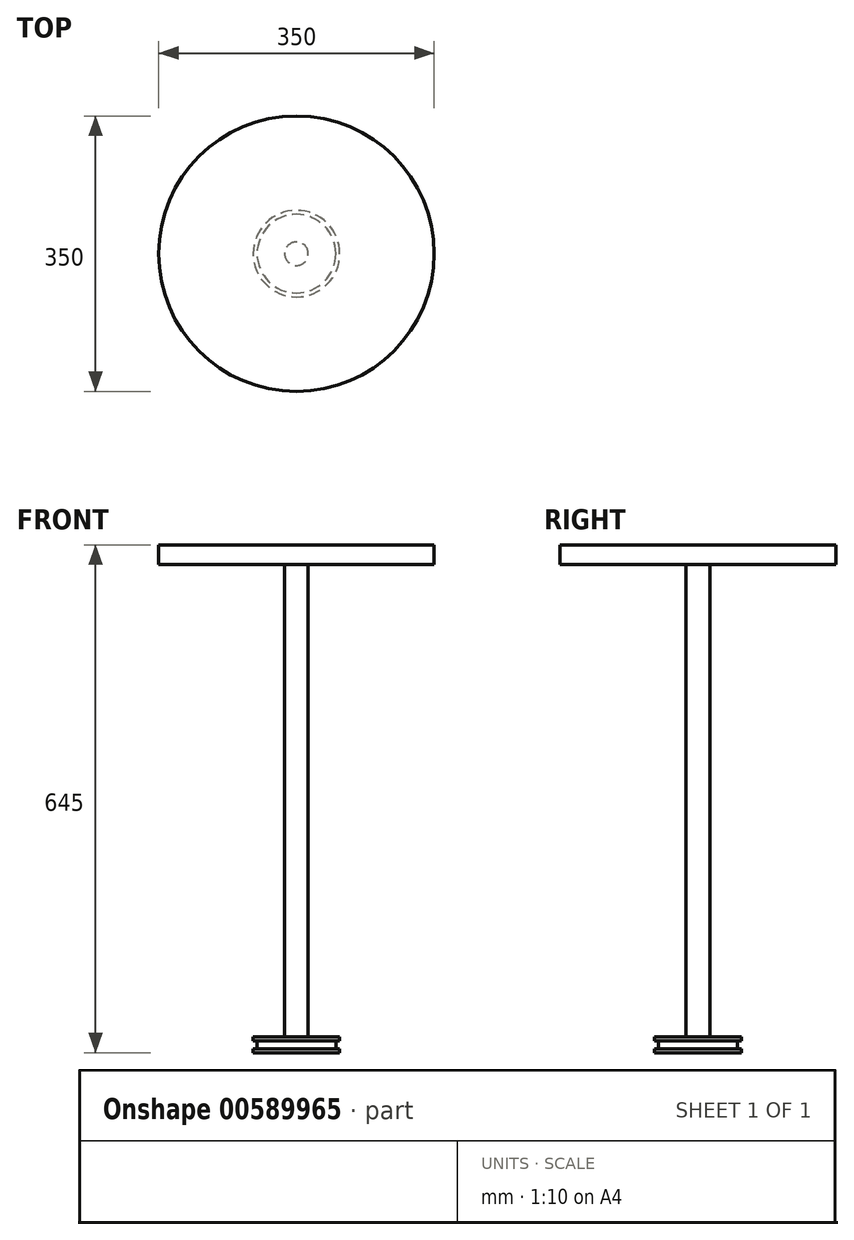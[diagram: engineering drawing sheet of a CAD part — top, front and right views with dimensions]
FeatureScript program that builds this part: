
annotation { "Feature Type Name" : "Feature", "Feature Type Description" : "" }
export const myFeature = defineFeature(function(context is Context, id is Id, definition is map)
    precondition{}
    {
        {
            var Q0;
            Q0=qCreatedBy(makeId("Top.planeOp"),FACE);
            var sketch = newSketch(context, id + "F0", { "sketchPlane" : qUnion([Q0])});
            skCircle(sketch, "E0", {"center": v(0, 0) * mm, "radius": 175 * mm});
            skSolve(sketch);
        }
        {
            var Q0;
            Q0 = qSketchRegion(id + "F0", true);
            extrude(context, id + "F1", {"entities" : qUnion([Q0]), "depth" : 25 * mm, "offsetDistance" : 25 * mm});
        }
        {
            var Q0;
            Q0=makeQuery(id+"F1.opExtrude","CAP_FACE",FACE,{"disambiguationData":[OSD([sQuery(id+"F0.wireOp",EDGE,"E0")])],"isStart":true});
            var sketch = newSketch(context, id + "F2", { "sketchPlane" : qUnion([Q0])});
            skCircle(sketch, "E1", {"center": v(0, 0) * mm, "radius": 15 * mm});
            skSolve(sketch);
        }
        {
            var Q0;
            Q0=makeQuery(id+"F2.imprint","IMPRINT",FACE,{"disambiguationData":[TD([[makeQuery(id+"F2.imprint","IMPRINT",EDGE,{"derivedFrom":sQuery(id+"F2.wireOp",EDGE,"E1")}),1.0]])]});
            extrude(context, id + "F3", {"entities" : qUnion([Q0]), "operationType" : NewBodyOperationType.ADD, "depth" : 600 * mm, "offsetDistance" : 25 * mm});
        }
        {
            var Q0;
            Q0=makeQuery(id+"F3.opExtrude","CAP_FACE",FACE,{"disambiguationData":[OSD([sQuery(id+"F2.wireOp",EDGE,"E1")])],"isStart":false});
            var sketch = newSketch(context, id + "F4", { "sketchPlane" : qUnion([Q0])});
            skCircle(sketch, "E2", {"center": v(0, 0) * mm, "radius": 55 * mm});
            skSolve(sketch);
        }
        {
            var Q0;
            Q0=makeQuery(id+"F4.imprint","IMPRINT",FACE,{"disambiguationData":[TD([[makeQuery(id+"F4.imprint","IMPRINT",EDGE,{"derivedFrom":makeQuery(id+"F3.opExtrude","CAP_EDGE",EDGE,{"disambiguationData":[OSD([sQuery(id+"F2.wireOp",EDGE,"E1")])],"isStart":false})}),1.0]])]});
            var Q1;
            Q1=makeQuery(id+"F4.imprint","IMPRINT",FACE,{"disambiguationData":[TD([[makeQuery(id+"F4.imprint","IMPRINT",EDGE,{"derivedFrom":sQuery(id+"F4.wireOp",EDGE,"E2")}),1.0]])]});
            extrude(context, id + "F5", {"entities" : qUnion([Q0, Q1]), "operationType" : NewBodyOperationType.ADD, "depth" : 5 * mm, "offsetDistance" : 25 * mm});
        }
        {
            var Q0;
            Q0=makeQuery(id+"F5.opExtrude","CAP_FACE",FACE,{"disambiguationData":[OSD([sQuery(id+"F4.wireOp",EDGE,"E2")])],"isStart":false});
            var sketch = newSketch(context, id + "F6", { "sketchPlane" : qUnion([Q0])});
            skCircle(sketch, "E3", {"center": v(0, 0) * mm, "radius": 50 * mm});
            skSolve(sketch);
        }
        {
            var Q0;
            Q0=makeQuery(id+"F6.imprint","IMPRINT",FACE,{"disambiguationData":[TD([[makeQuery(id+"F6.imprint","IMPRINT",EDGE,{"derivedFrom":sQuery(id+"F6.wireOp",EDGE,"E3")}),1.0]])]});
            extrude(context, id + "F7", {"entities" : qUnion([Q0]), "operationType" : NewBodyOperationType.ADD, "depth" : 10 * mm, "offsetDistance" : 25 * mm});
        }
        {
            var Q0;
            Q0=makeQuery(id+"F7.opExtrude","CAP_FACE",FACE,{"disambiguationData":[OSD([sQuery(id+"F6.wireOp",EDGE,"E3")])],"isStart":false});
            var sketch = newSketch(context, id + "F8", { "sketchPlane" : qUnion([Q0])});
            skCircle(sketch, "E4", {"center": v(0, 0) * mm, "radius": 55 * mm});
            skSolve(sketch);
        }
        {
            var Q0;
            Q0=makeQuery(id+"F8.imprint","IMPRINT",FACE,{"disambiguationData":[TD([[makeQuery(id+"F8.imprint","IMPRINT",EDGE,{"derivedFrom":sQuery(id+"F8.wireOp",EDGE,"E4")}),1.0]])]});
            var Q1;
            Q1=makeQuery(id+"F8.imprint","IMPRINT",FACE,{"disambiguationData":[TD([[makeQuery(id+"F8.imprint","IMPRINT",EDGE,{"derivedFrom":makeQuery(id+"F7.opExtrude","CAP_EDGE",EDGE,{"disambiguationData":[OSD([sQuery(id+"F6.wireOp",EDGE,"E3")])],"isStart":false})}),1.0]])]});
            extrude(context, id + "F9", {"entities" : qUnion([Q0, Q1]), "operationType" : NewBodyOperationType.ADD, "depth" : 5 * mm, "offsetDistance" : 25 * mm});
        }
    });
